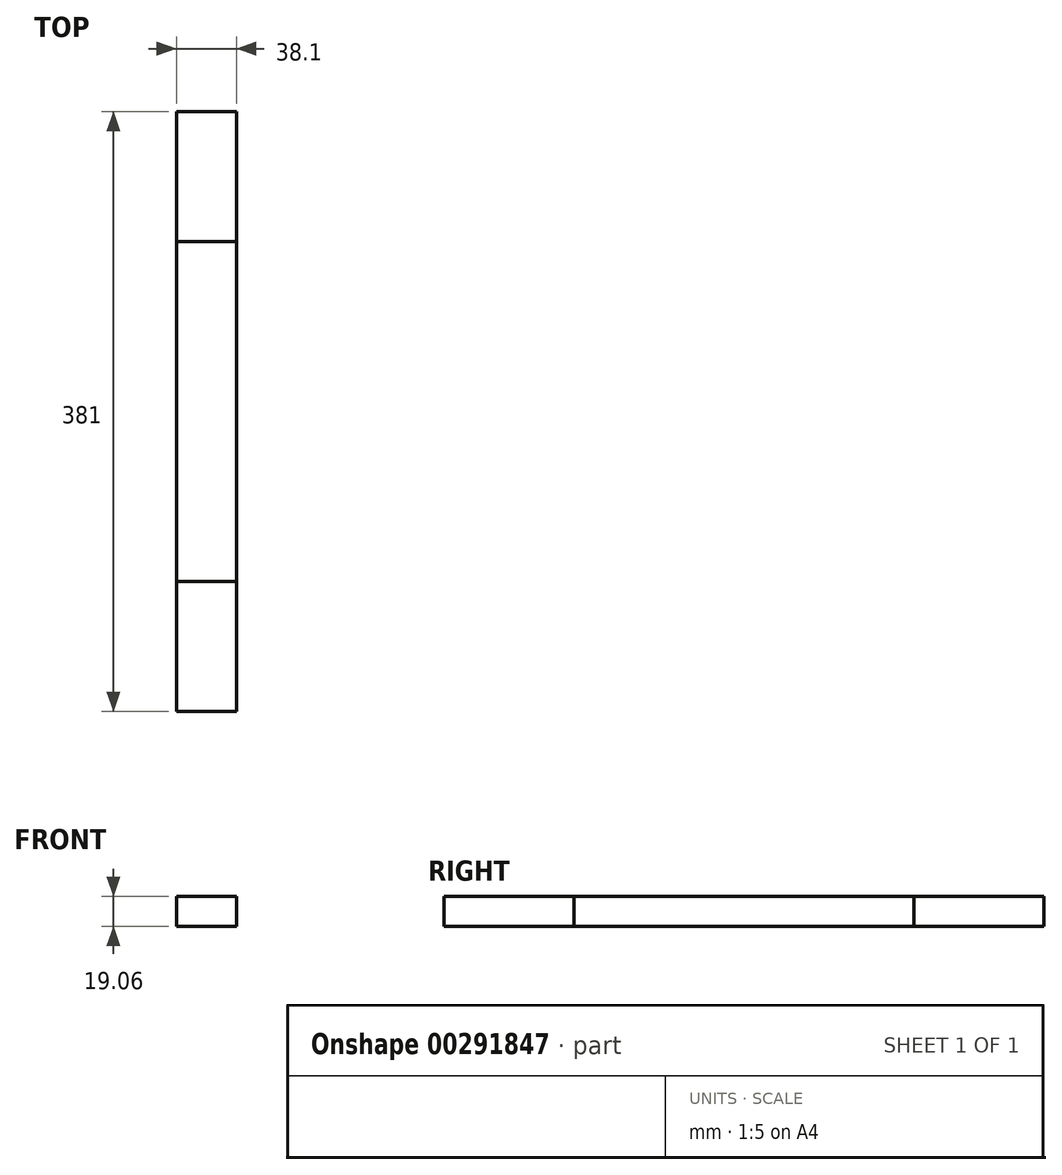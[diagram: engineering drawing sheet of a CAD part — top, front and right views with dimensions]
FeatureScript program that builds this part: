
annotation { "Feature Type Name" : "Feature", "Feature Type Description" : "" }
export const myFeature = defineFeature(function(context is Context, id is Id, definition is map)
    precondition{}
    {
        {
            var Q0;
            Q0=qCreatedBy(makeId("Front.planeOp"),FACE);
            var sketch = newSketch(context, id + "F0", { "sketchPlane" : qUnion([Q0])});
            skLineSegment(sketch, "E0.bottom", {"start": v(19.05, -9.53) * mm, "end": v(-19.05, -9.53) * mm});
            skLineSegment(sketch, "E0.top", {"start": v(19.05, 9.53) * mm, "end": v(-19.05, 9.53) * mm});
            skLineSegment(sketch, "E0.left", {"start": v(19.05, -9.53) * mm, "end": v(19.05, 9.52) * mm});
            skLineSegment(sketch, "E0.right", {"start": v(-19.05, -9.53) * mm, "end": v(-19.05, 9.52) * mm});
            skPoint(sketch, "E0.middle", {"position": v(0, 0) * mm});
            skSolve(sketch);
        }
        {
            var Q0;
            Q0 = qSketchRegion(id + "F0", true);
            extrude(context, id + "F1", {"entities" : qUnion([Q0]), "endBound" : BoundingType.SYMMETRIC, "depth" : 215.9 * mm});
        }
        {
            var Q0;
            Q0 = qSketchRegion(id + "F0", true);
            extrude(context, id + "F2", {"entities" : qUnion([Q0]), "endBound" : BoundingType.SYMMETRIC, "depth" : 381 * mm});
        }
    });
